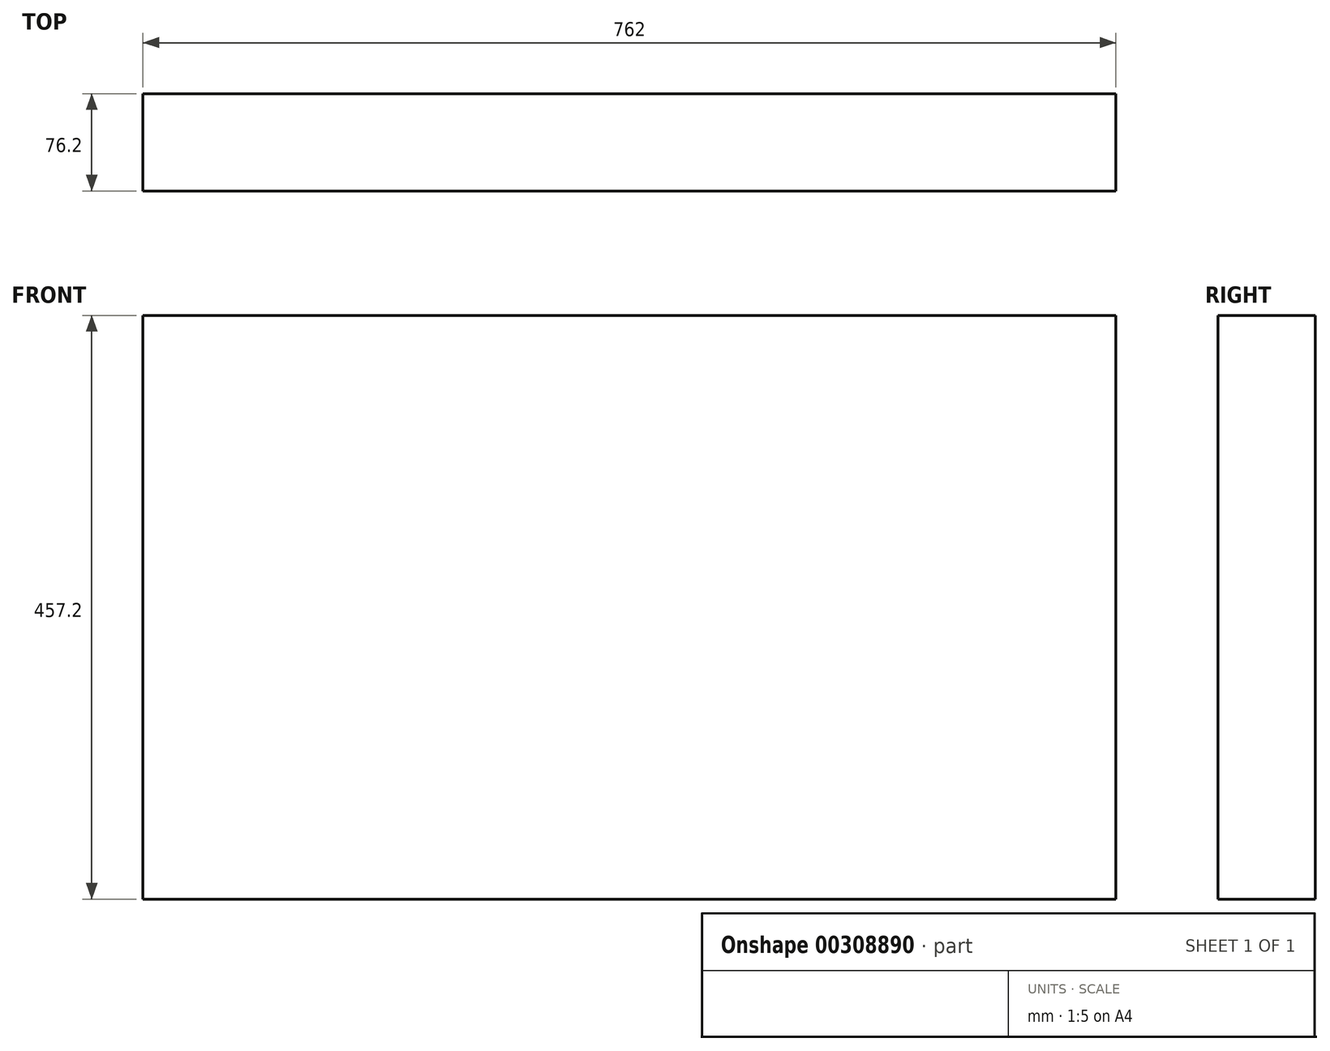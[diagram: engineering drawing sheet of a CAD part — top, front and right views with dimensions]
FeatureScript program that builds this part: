
annotation { "Feature Type Name" : "Feature", "Feature Type Description" : "" }
export const myFeature = defineFeature(function(context is Context, id is Id, definition is map)
    precondition{}
    {
        {
            var Q0;
            Q0=qCreatedBy(makeId("Front.planeOp"),FACE);
            var sketch = newSketch(context, id + "F0", { "sketchPlane" : qUnion([Q0])});
            skLineSegment(sketch, "E0.bottom", {"start": v(381, -228.6) * mm, "end": v(-381, -228.6) * mm});
            skLineSegment(sketch, "E0.top", {"start": v(381, 228.6) * mm, "end": v(-381, 228.6) * mm});
            skLineSegment(sketch, "E0.left", {"start": v(381, -228.6) * mm, "end": v(381, 228.6) * mm});
            skLineSegment(sketch, "E0.right", {"start": v(-381, -228.6) * mm, "end": v(-381, 228.6) * mm});
            skPoint(sketch, "E0.middle", {"position": v(0, 0) * mm});
            skSolve(sketch);
        }
        {
            var Q0;
            Q0=makeQuery(id+"F0.imprint","IMPRINT",FACE,{"disambiguationData":[TD([[makeQuery(id+"F0.imprint","IMPRINT",EDGE,{"derivedFrom":sQuery(id+"F0.wireOp",EDGE,"E0.bottom")}),-1.0]])]});
            extrude(context, id + "F1", {"entities" : qUnion([Q0]), "depth" : 76.2 * mm});
        }
    });
